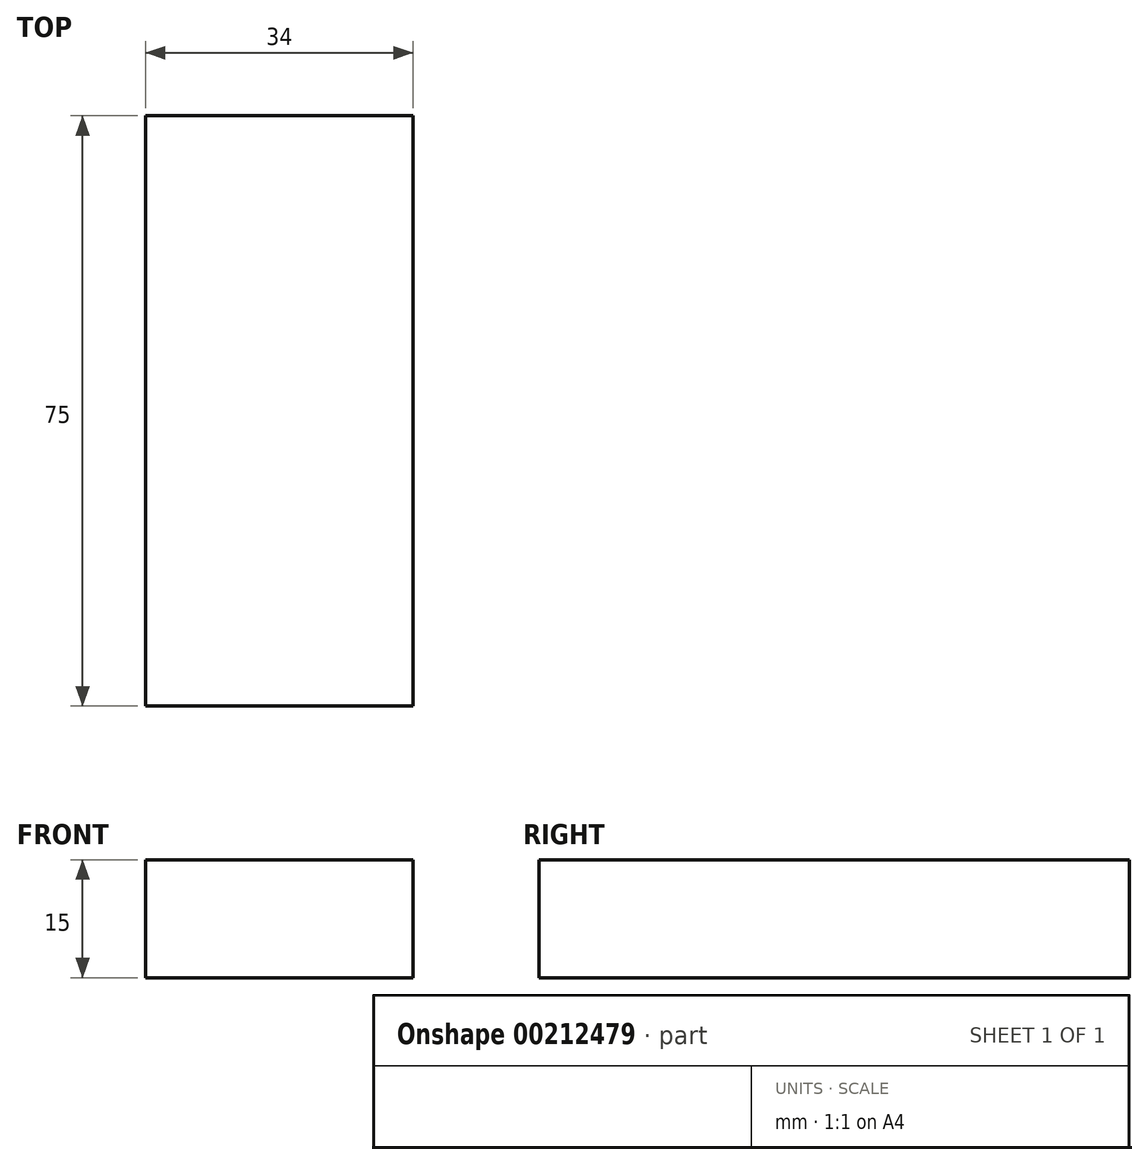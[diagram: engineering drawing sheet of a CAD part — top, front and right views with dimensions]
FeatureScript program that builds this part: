
annotation { "Feature Type Name" : "Feature", "Feature Type Description" : "" }
export const myFeature = defineFeature(function(context is Context, id is Id, definition is map)
    precondition{}
    {
        {
            var Q0;
            Q0=qCreatedBy(makeId("Top.planeOp"),FACE);
            var sketch = newSketch(context, id + "F0", { "sketchPlane" : qUnion([Q0])});
            skLineSegment(sketch, "E0.bottom", {"start": v(0, 0) * mm, "end": v(34, 0) * mm});
            skLineSegment(sketch, "E0.top", {"start": v(0, 75) * mm, "end": v(34, 75) * mm});
            skLineSegment(sketch, "E0.left", {"start": v(0, 0) * mm, "end": v(0, 75) * mm});
            skLineSegment(sketch, "E0.right", {"start": v(34, 0) * mm, "end": v(34, 75) * mm});
            skSolve(sketch);
        }
        {
            var Q0;
            Q0 = qSketchRegion(id + "F0", true);
            extrude(context, id + "F1", {"entities" : qUnion([Q0]), "depth" : 15 * mm});
        }
    });
